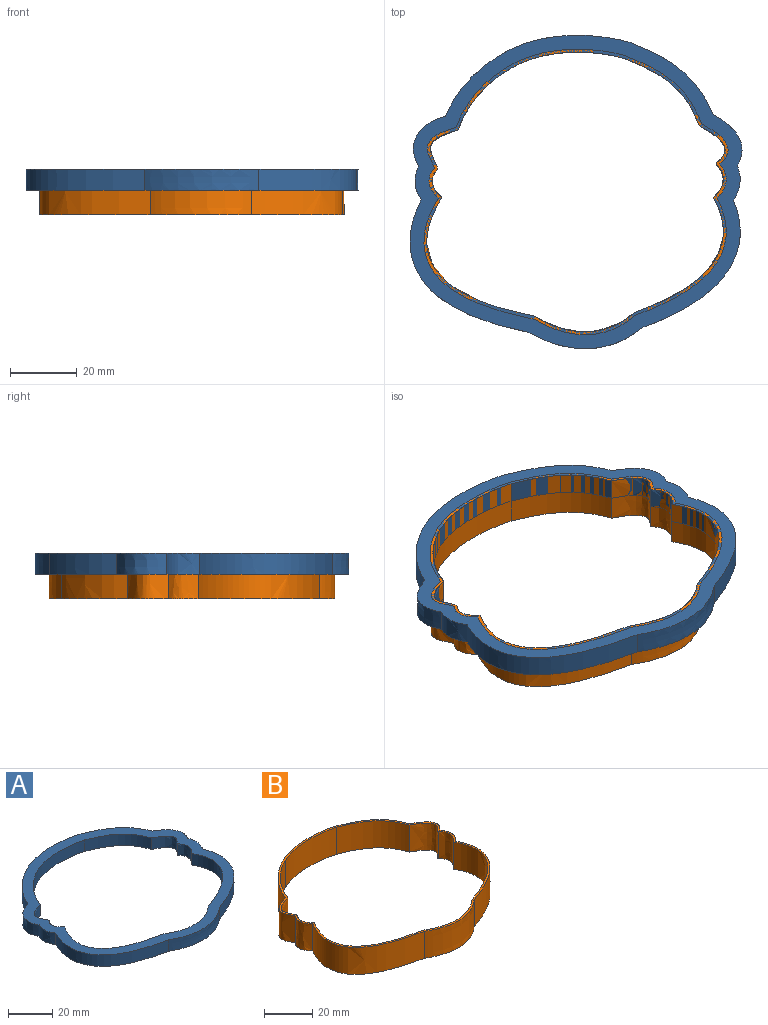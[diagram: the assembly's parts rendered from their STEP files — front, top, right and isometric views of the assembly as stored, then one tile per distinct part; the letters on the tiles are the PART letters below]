
ASSEMBLY  parts=2 mates=1
PART A: 22 faces, bbox 101.1x95.5x7.6 mm
  f0: plane 101.11x95.53mm, normal (0,0,1), area 1517.9mm2, adj f2,f3,f4,f5,f6,f7,f8,f9
  f1: plane 101.11x95.53mm, normal (0,0,-1), area 1517.9mm2, adj f2,f3,f4,f5,f6,f7,f8,f9
  f2: extruded ~20.17x19.77mm, area 183.2mm2, adj f0,f1,f3,f11
  f3: extruded ~15.21x9.59mm, area 129.7mm2, adj f0,f1,f2,f4
  f4: extruded ~9.94x6.35mm, area 66.7mm2, adj f0,f1,f3,f5
  f5: extruded ~39.88x35.75mm, area 393.9mm2, adj f0,f1,f4,f6
  f6: extruded ~34.26x6.44mm, area 233.1mm2, adj f0,f1,f5,f7
  f7: extruded ~38.19x29.24mm, area 339.3mm2, adj f0,f1,f6,f8
  f8: extruded ~10.5x6.35mm, area 70mm2, adj f0,f1,f7,f9
  f9: extruded ~15.48x8.85mm, area 124.5mm2, adj f0,f1,f8,f10
  f10: extruded ~24.8x21.46mm, area 215.2mm2, adj f0,f1,f9,f11
  f11: extruded ~35.79x6.35mm, area 232.4mm2, adj f0,f1,f2,f10
  f12: extruded ~19.81x18.24mm, area 175.4mm2, adj f0,f1,f13,f21
  f13: extruded ~11.77x8.28mm, area 109.6mm2, adj f0,f1,f12,f14
  f14: extruded ~8.48x6.35mm, area 63.5mm2, adj f0,f1,f13,f15
  f15: extruded ~35.77x32.53mm, area 361.9mm2, adj f0,f1,f14,f16
  f16: extruded ~29.83x6.35mm, area 204.4mm2, adj f0,f1,f15,f17
  f17: extruded ~34.61x26.75mm, area 313mm2, adj f0,f1,f16,f18
  f18: extruded ~9.94x6.35mm, area 73.5mm2, adj f0,f1,f17,f19
  f19: extruded ~11.54x7.81mm, area 103.4mm2, adj f0,f1,f18,f20
  f20: extruded ~22.37x20.24mm, area 199mm2, adj f0,f1,f19,f21
  f21: extruded ~31.92x6.35mm, area 207.1mm2, adj f0,f1,f12,f20
PART B: 22 faces, bbox 101.8x90.9x18.2 mm
  f0: plane 101.83x90.92mm, normal (0,0,1), area 255.2mm2, adj f2,f3,f4,f5,f6,f7,f8,f9
  f1: plane 101.83x90.92mm, normal (0,0,-1), area 255.2mm2, adj f2,f3,f4,f5,f6,f7,f8,f9
  f2: extruded ~19.86x18.52mm, area 381.6mm2, adj f0,f1,f3,f11
  f3: extruded ~13.72x12.22mm, area 242.2mm2, adj f0,f1,f2,f4
  f4: extruded ~13.72x8.95mm, area 140.6mm2, adj f0,f1,f3,f5
  f5: extruded ~36.44x33.1mm, area 792.7mm2, adj f0,f1,f4,f6
  f6: extruded ~30.61x13.72mm, area 452.5mm2, adj f0,f1,f5,f7
  f7: extruded ~35.14x27.17mm, area 684.3mm2, adj f0,f1,f6,f8
  f8: extruded ~13.72x10.28mm, area 158.8mm2, adj f0,f1,f7,f9
  f9: extruded ~13.72x12.09mm, area 229.3mm2, adj f0,f1,f8,f10
  f10: extruded ~22.8x20.45mm, area 436mm2, adj f0,f1,f9,f11
  f11: extruded ~32.6x13.72mm, area 456.9mm2, adj f0,f1,f2,f10
  f12: extruded ~19.81x18.24mm, area 378.8mm2, adj f0,f1,f13,f21
  f13: extruded ~13.72x11.77mm, area 236.7mm2, adj f0,f1,f12,f14
  f14: extruded ~13.72x8.48mm, area 137.1mm2, adj f0,f1,f13,f15
  f15: extruded ~35.77x32.53mm, area 781.6mm2, adj f0,f1,f14,f16
  f16: extruded ~29.83x13.72mm, area 441.6mm2, adj f0,f1,f15,f17
  f17: extruded ~34.61x26.75mm, area 676mm2, adj f0,f1,f16,f18
  f18: extruded ~13.72x9.94mm, area 158.7mm2, adj f0,f1,f17,f19
  f19: extruded ~13.72x11.54mm, area 223.4mm2, adj f0,f1,f18,f20
  f20: extruded ~22.37x20.24mm, area 429.9mm2, adj f0,f1,f19,f21
  f21: extruded ~31.92x13.72mm, area 447.3mm2, adj f0,f1,f12,f20
PLACE A at identity
PLACE B t=(118.09,2.9,-7.37)mm
MATE fastened B.f0 <-> A.f0  axis (0,0,1) through (85.6,4.5,6.35)mm
